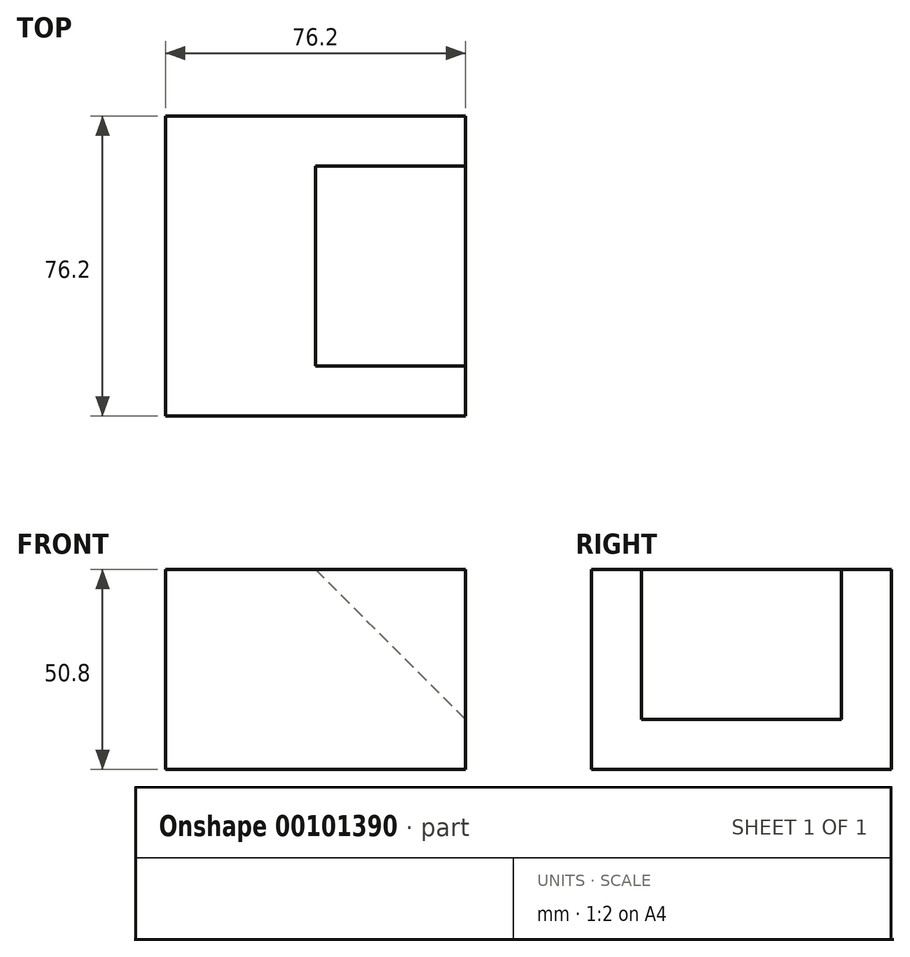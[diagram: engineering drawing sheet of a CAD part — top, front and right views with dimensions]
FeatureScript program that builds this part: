
annotation { "Feature Type Name" : "Feature", "Feature Type Description" : "" }
export const myFeature = defineFeature(function(context is Context, id is Id, definition is map)
    precondition{}
    {
        {
            var Q0;
            Q0=qCreatedBy(makeId("Front.planeOp"),FACE);
            var sketch = newSketch(context, id + "F0", { "sketchPlane" : qUnion([Q0])});
            skLineSegment(sketch, "E0", {"start": v(0, 0) * mm, "end": v(0, 50.8) * mm});
            skLineSegment(sketch, "E1", {"start": v(0, 50.8) * mm, "end": v(76.2, 50.8) * mm});
            skLineSegment(sketch, "E2", {"start": v(76.2, 50.8) * mm, "end": v(76.2, 0) * mm});
            skLineSegment(sketch, "E3", {"start": v(76.2, 0) * mm, "end": v(0, 0) * mm});
            skSolve(sketch);
        }
        {
            var Q0;
            Q0=qCreatedBy(makeId("Front.planeOp"),FACE);
            var sketch = newSketch(context, id + "F1", { "sketchPlane" : qUnion([Q0])});
            skLineSegment(sketch, "E4", {"start": v(38.1, 50.8) * mm, "end": v(76.2, 12.7) * mm});
            skLineSegment(sketch, "E5", {"start": v(38.1, 50.8) * mm, "end": v(76.2, 50.8) * mm});
            skLineSegment(sketch, "E6", {"start": v(76.2, 50.8) * mm, "end": v(76.2, 12.7) * mm});
            skSolve(sketch);
        }
        {
            var Q0;
            Q0 = qSketchRegion(id + "F0", true);
            extrude(context, id + "F2", {"entities" : qUnion([Q0]), "endBound" : BoundingType.SYMMETRIC, "depth" : 76.2 * mm});
        }
        {
            var Q0;
            Q0 = qSketchRegion(id + "F1", true);
            extrude(context, id + "F3", {"entities" : qUnion([Q0]), "operationType" : NewBodyOperationType.REMOVE, "endBound" : BoundingType.SYMMETRIC, "depth" : 50.8 * mm});
        }
    });
